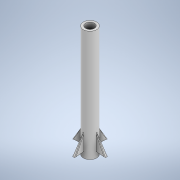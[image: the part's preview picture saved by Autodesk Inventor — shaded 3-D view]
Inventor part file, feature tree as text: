
AUTODESK INVENTOR PART (.ipt)
format: ipt  version: 2022 (Build 260153000, 153)  size: 239,616 bytes
history: native  units: in
note: dims shown in document units (in); Inventor stores cm internally (conversion verified against a paired STEP export)
features: revolve x2, fillet x2, sketch x2, pattern_circular x1
ambient origin geometry x8: Origin, YZ Plane, XZ Plane, XY Plane, X Axis, Y Axis, Z Axis, Center Point
bodies: Solid1 (feature_tree)
feature tree (7):
  revolve  "Revolution1"  [1 undecoded]
  revolve  "Revolution3"  [1 undecoded]
  pattern_circular  "Circular Pattern1"  Angle=90.0deg  [1 undecoded]
  fillet  "Fillet1"  Radius=0.5906in
  fillet  "Fillet2"  [1 undecoded]
  sketch  "Sketch2"  dims[d0=3.937in d1=0.315in]
  sketch  "Sketch4"  dims[d2=3.937in d3=0.4724in d4=90.0deg d10=0.5906in d11=30.0deg d12=0.0687in d13=1.5748in d14=360.0deg d16=0.0197in d17=0.0197in]
note: 4 required parameter values undecoded (feature->parameter linkage not recoverable at this tier; creation-order binding heuristic only, values carry confidence <= 0.55)